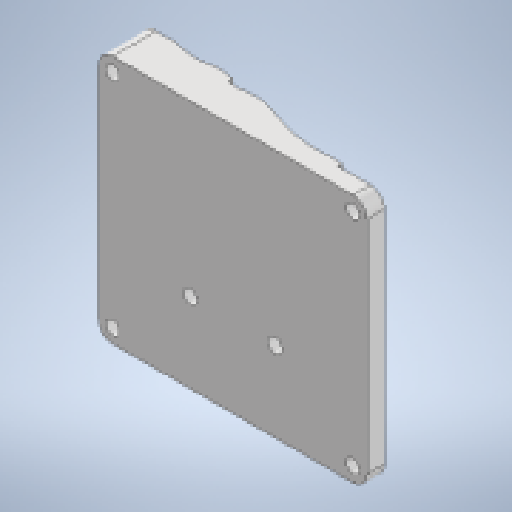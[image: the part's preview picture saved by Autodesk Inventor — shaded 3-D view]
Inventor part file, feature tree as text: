
AUTODESK INVENTOR PART (.ipt)
format: ipt  version: 2023 (Build 270158000, 158)  size: 265,728 bytes
history: native  units: mm
features: other x7, reference x6, extrude x3, sketch x2, plane x1, fillet x1
ambient origin geometry x8: Origin, YZ Plane, XZ Plane, XY Plane, X Axis, Y Axis, Z Axis, Center Point
bodies: Solid1 (feature_tree)
feature tree (20):
  plane  "Work Plane1"
  extrude  "Extrusion1"  Depth=22.0mm
  extrude  "Extrusion2"  Depth=3.0mm
  fillet  "Fillet1"  Radius=2.9mm
  extrude  "Extrusion3"  Depth=21.749mm TaperAngle=0.0deg
  reference  "Reference3"
  reference  "Reference4"
  sketch  "Sketch2"  dims[d0=10.15mm d1=22.0mm]
  reference  "Reference6"
  reference  "Reference7"
  sketch  "Sketch3"  dims[d2=3.0mm d3=3.0mm d4=2.9mm d13=21.749mm d14=0.0mm d15=0.0mm d16=0.0mm d17=3.0mm d18=0.0mm d19=67.251mm d20=0.0mm d23=0.5mm d24=0.5mm d26=20.0mm d28=51.188mm d29=20.0mm d31=47.043mm]
  reference  "Reference10"
  reference  "Reference11"
  parser-record x1  (decoder bookkeeping rows leaked as tree rows — omitted from the tree; the rows remain in map.json)
  other  "Assembly_V6.iam"
  other  "rack_V6:1"
  other  "pinion_V6:2"
  other  "moulding:1"
  other  "motor:2"
  other  "motor:1"
note: 1 file-system path scrubbed to <path> (originals preserved in map.json)
